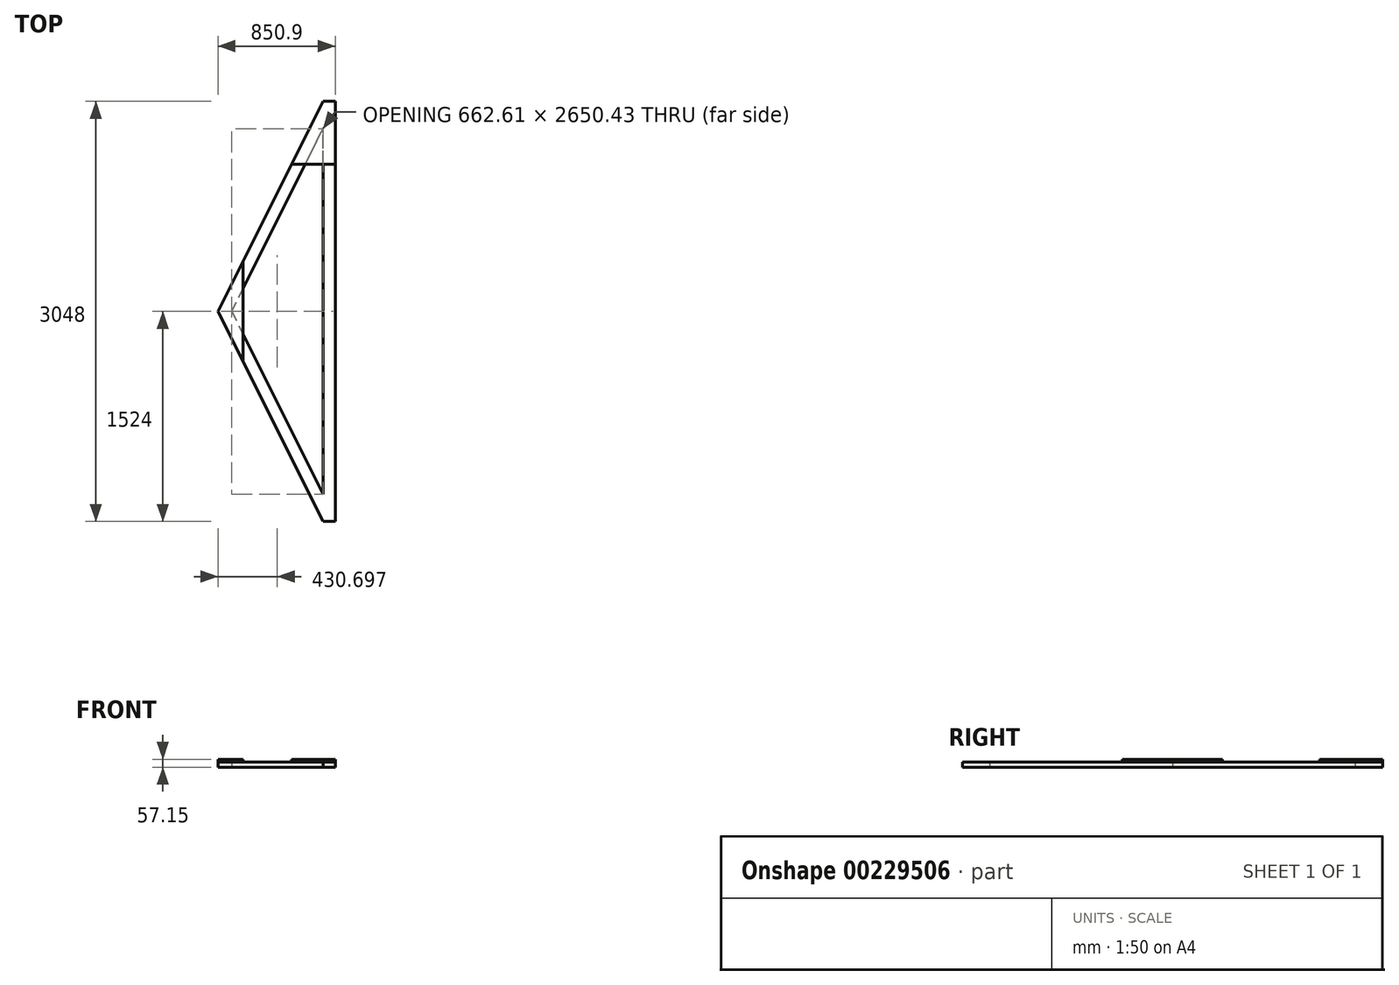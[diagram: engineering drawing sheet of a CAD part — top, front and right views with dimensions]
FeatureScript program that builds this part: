
annotation { "Feature Type Name" : "Feature", "Feature Type Description" : "" }
export const myFeature = defineFeature(function(context is Context, id is Id, definition is map)
    precondition{}
    {
        {
            var Q0;
            Q0=qCreatedBy(makeId("Front.planeOp"),FACE);
            var sketch = newSketch(context, id + "F0", { "sketchPlane" : qUnion([Q0])});
            skLineSegment(sketch, "E0.bottom", {"start": v(0, 0) * mm, "end": v(88.9, 0) * mm});
            skLineSegment(sketch, "E0.top", {"start": v(0, -38.1) * mm, "end": v(88.9, -38.1) * mm});
            skLineSegment(sketch, "E0.left", {"start": v(0, 0) * mm, "end": v(0, -38.1) * mm});
            skLineSegment(sketch, "E0.right", {"start": v(88.9, 0) * mm, "end": v(88.9, -38.1) * mm});
            skSolve(sketch);
        }
        {
            var Q0;
            Q0=qSketchRegion(id+"F0",true);
            extrude(context, id + "F1", {"entities" : qUnion([Q0]), "depth" : 3048 * mm});
        }
        {
            var Q0;
            Q0=qCreatedBy(makeId("Top.planeOp"),FACE);
            var sketch = newSketch(context, id + "F2", { "sketchPlane" : qUnion([Q0])});
            skLineSegment(sketch, "E1", {"start": v(0, 0) * mm, "end": v(-762, -1524) * mm});
            skLineSegment(sketch, "E2", {"start": v(-762, -1524) * mm, "end": v(-682.49, -1563.76) * mm});
            skLineSegment(sketch, "E3", {"start": v(-682.49, -1563.76) * mm, "end": v(79.51, -39.76) * mm});
            skLineSegment(sketch, "E4", {"start": v(0, 0) * mm, "end": v(79.51, -39.76) * mm});
            skSolve(sketch);
        }
        {
            var Q0;
            Q0=makeQuery(id+"F2.imprint","IMPRINT",FACE,{"disambiguationData":[TD([[makeQuery(id+"F2.imprint","IMPRINT",EDGE,{"derivedFrom":sQuery(id+"F2.wireOp",EDGE,"E1")}),1.0]])]});
            extrude(context, id + "F3", {"entities" : qUnion([Q0]), "operationType" : NewBodyOperationType.ADD, "oppositeDirection" : true, "depth" : 38.1 * mm});
        }
        {
            var Q0;
            Q0=qCreatedBy(makeId("Top.planeOp"),FACE);
            var sketch = newSketch(context, id + "F4", { "sketchPlane" : qUnion([Q0])});
            skPoint(sketch, "E5.0", {"position": v(-762, -1524) * mm});
            skPoint(sketch, "E6.0", {"position": v(0, -3048) * mm});
            skLineSegment(sketch, "E7", {"start": v(-762, -1524) * mm, "end": v(0, -3048) * mm});
            skLineSegment(sketch, "E8", {"start": v(-762, -1524) * mm, "end": v(-682.49, -1484.24) * mm});
            skLineSegment(sketch, "E9", {"start": v(-682.49, -1484.24) * mm, "end": v(79.51, -3008.24) * mm});
            skLineSegment(sketch, "E10", {"start": v(0, -3048) * mm, "end": v(79.51, -3008.24) * mm});
            skSolve(sketch);
        }
        {
            var Q0;
            Q0 = qSketchRegion(id + "F4", true);
            extrude(context, id + "F5", {"entities" : qUnion([Q0]), "operationType" : NewBodyOperationType.ADD, "oppositeDirection" : true, "depth" : 38.1 * mm});
        }
        {
            var Q0;
            Q0=makeQuery(id+"F5.boolean.opBoolean","MERGE",FACE,{"derivedFrom":[makeQuery(id+"F3.boolean.opBoolean","MERGE",FACE,{"derivedFrom":[makeQuery(id+"F1.opExtrude","SWEPT_FACE",FACE,{"disambiguationData":[OSD([sQuery(id+"F0.wireOp",EDGE,"E0.bottom")])]}),makeQuery(id+"F3.opExtrude","CAP_FACE",FACE,{"disambiguationData":[OSD([sQuery(id+"F2.wireOp",EDGE,"E1"),sQuery(id+"F2.wireOp",EDGE,"E2"),sQuery(id+"F2.wireOp",EDGE,"E3"),sQuery(id+"F2.wireOp",EDGE,"E4")])],"isStart":true})]}),makeQuery(id+"F5.opExtrude","CAP_FACE",FACE,{"disambiguationData":[OSD([sQuery(id+"F4.wireOp",EDGE,"E7"),sQuery(id+"F4.wireOp",EDGE,"E8"),sQuery(id+"F4.wireOp",EDGE,"E9"),sQuery(id+"F4.wireOp",EDGE,"E10")])],"isStart":true})]});
            var sketch = newSketch(context, id + "F6", { "sketchPlane" : qUnion([Q0])});
            skLineSegment(sketch, "E11.0.0", {"start": v(0, 0) * mm, "end": v(-762, -1524) * mm, "construction": true});
            skLineSegment(sketch, "E11.0.1", {"start": v(-762, -1524) * mm, "end": v(0, -3048) * mm, "construction": true});
            skLineSegment(sketch, "E11.0.2", {"start": v(0, -3048) * mm, "end": v(88.9, -3048) * mm, "construction": true});
            skLineSegment(sketch, "E11.0.3", {"start": v(88.9, -3048) * mm, "end": v(88.9, 0) * mm, "construction": true});
            skLineSegment(sketch, "E11.0.4", {"start": v(88.9, 0) * mm, "end": v(0, 0) * mm, "construction": true});
            skLineSegment(sketch, "E12", {"start": v(88.9, -457.2) * mm, "end": v(-228.6, -457.2) * mm});
            skLineSegment(sketch, "E13", {"start": v(-228.6, -457.2) * mm, "end": v(0, 0) * mm});
            skLineSegment(sketch, "E14", {"start": v(88.9, 0) * mm, "end": v(88.9, -457.2) * mm});
            skLineSegment(sketch, "E15", {"start": v(0, 0) * mm, "end": v(88.9, 0) * mm});
            skSolve(sketch);
        }
        {
            var Q0;
            Q0 = qSketchRegion(id + "F6", true);
            extrude(context, id + "F7", {"entities" : qUnion([Q0]), "depth" : 19.05 * mm});
        }
        {
            var Q0;
            Q0=makeQuery(id+"F5.boolean.opBoolean","MERGE",FACE,{"derivedFrom":[makeQuery(id+"F3.boolean.opBoolean","MERGE",FACE,{"derivedFrom":[makeQuery(id+"F1.opExtrude","SWEPT_FACE",FACE,{"disambiguationData":[OSD([sQuery(id+"F0.wireOp",EDGE,"E0.bottom")])]}),makeQuery(id+"F3.opExtrude","CAP_FACE",FACE,{"disambiguationData":[OSD([sQuery(id+"F2.wireOp",EDGE,"E1"),sQuery(id+"F2.wireOp",EDGE,"E2"),sQuery(id+"F2.wireOp",EDGE,"E3"),sQuery(id+"F2.wireOp",EDGE,"E4")])],"isStart":true})]}),makeQuery(id+"F5.opExtrude","CAP_FACE",FACE,{"disambiguationData":[OSD([sQuery(id+"F4.wireOp",EDGE,"E7"),sQuery(id+"F4.wireOp",EDGE,"E8"),sQuery(id+"F4.wireOp",EDGE,"E9"),sQuery(id+"F4.wireOp",EDGE,"E10")])],"isStart":true})]});
            var sketch = newSketch(context, id + "F8", { "sketchPlane" : qUnion([Q0])});
            skLineSegment(sketch, "E16.0", {"start": v(0, 0) * mm, "end": v(-762, -1524) * mm, "construction": true});
            skLineSegment(sketch, "E17.0", {"start": v(-762, -1524) * mm, "end": v(0, -3048) * mm, "construction": true});
            skLineSegment(sketch, "E18.0", {"start": v(88.9, -3048) * mm, "end": v(88.9, 0) * mm, "construction": true});
            skLineSegment(sketch, "E19", {"start": v(-762, -1524) * mm, "end": v(-580.25, -1160.5) * mm});
            skLineSegment(sketch, "E20", {"start": v(-762, -1524) * mm, "end": v(-580.25, -1887.5) * mm});
            skLineSegment(sketch, "E21", {"start": v(-580.25, -1887.5) * mm, "end": v(-580.25, -1160.5) * mm});
            skSolve(sketch);
        }
        {
            var Q0;
            Q0 = qSketchRegion(id + "F8", true);
            extrude(context, id + "F9", {"entities" : qUnion([Q0]), "depth" : 19.05 * mm});
        }
    });
